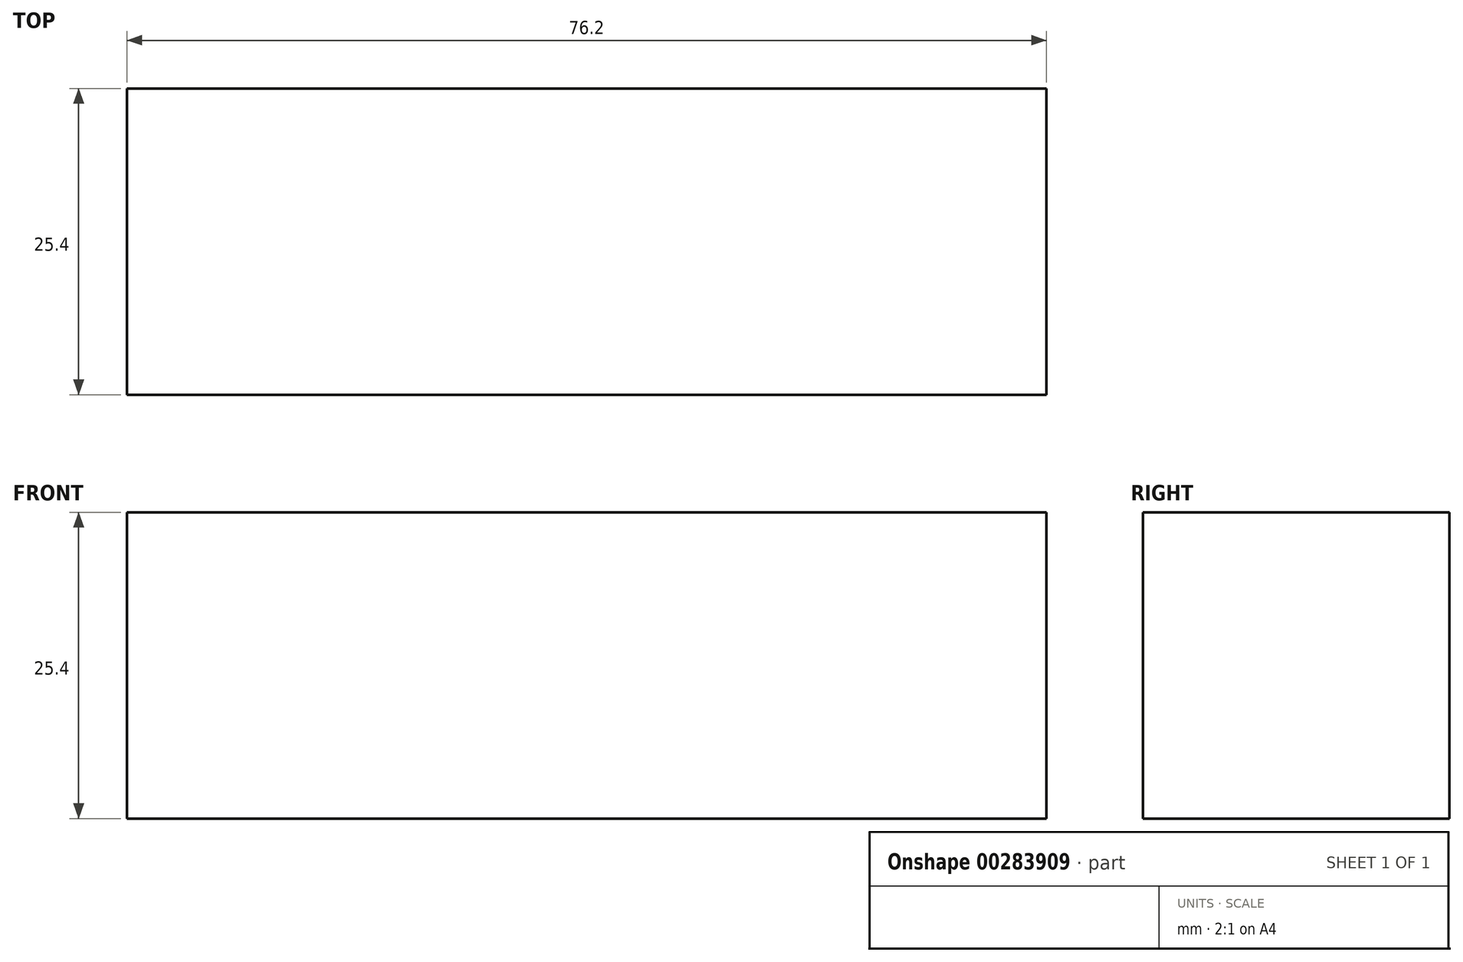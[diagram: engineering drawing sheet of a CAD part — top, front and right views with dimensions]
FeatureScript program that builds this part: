
annotation { "Feature Type Name" : "Feature", "Feature Type Description" : "" }
export const myFeature = defineFeature(function(context is Context, id is Id, definition is map)
    precondition{}
    {
        {
            var Q0;
            Q0=qCreatedBy(makeId("Right.planeOp"),FACE);
            var sketch = newSketch(context, id + "F0", { "sketchPlane" : qUnion([Q0])});
            skLineSegment(sketch, "E0.bottom", {"start": v(0, 0) * mm, "end": v(-25.4, 0) * mm});
            skLineSegment(sketch, "E0.top", {"start": v(0, 25.4) * mm, "end": v(-25.4, 25.4) * mm});
            skLineSegment(sketch, "E0.left", {"start": v(0, 0) * mm, "end": v(0, 25.4) * mm});
            skLineSegment(sketch, "E0.right", {"start": v(-25.4, 0) * mm, "end": v(-25.4, 25.4) * mm});
            skSolve(sketch);
        }
        {
            var Q0;
            Q0 = qSketchRegion(id + "F0", true);
            extrude(context, id + "F1", {"entities" : qUnion([Q0]), "depth" : 76.2 * mm});
        }
    });
